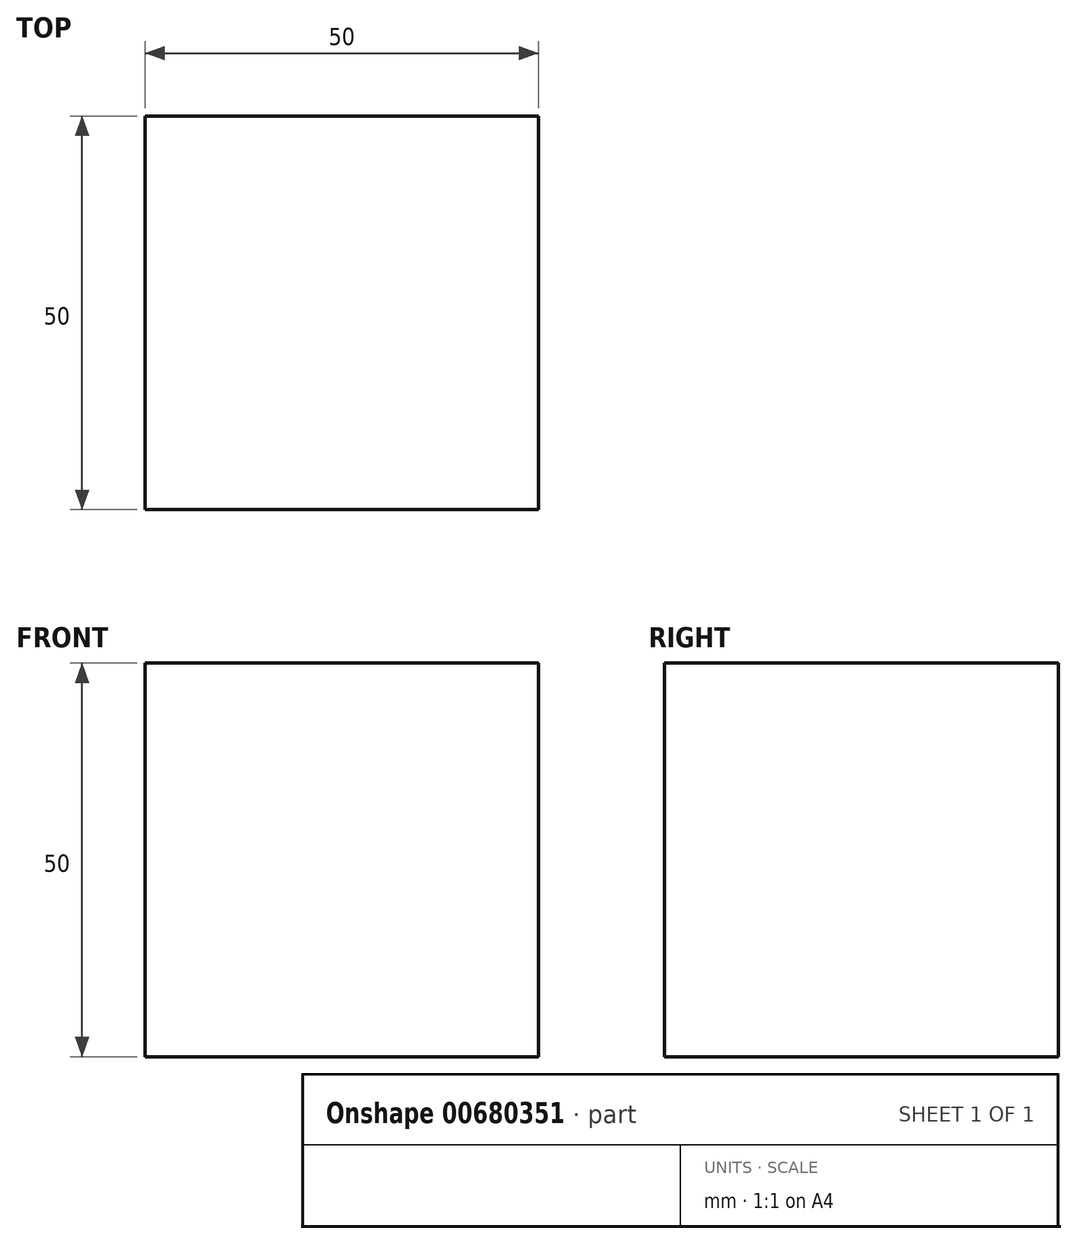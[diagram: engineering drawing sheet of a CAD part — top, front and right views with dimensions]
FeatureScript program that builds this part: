
annotation { "Feature Type Name" : "Feature", "Feature Type Description" : "" }
export const myFeature = defineFeature(function(context is Context, id is Id, definition is map)
    precondition{}
    {
        {
            var Q0;
            Q0=qCreatedBy(makeId("Top.planeOp"),FACE);
            var sketch = newSketch(context, id + "F0", { "sketchPlane" : qUnion([Q0])});
            skLineSegment(sketch, "E0.bottom", {"start": v(-22.73, 17.37) * mm, "end": v(27.27, 17.37) * mm});
            skLineSegment(sketch, "E0.top", {"start": v(-22.73, -32.63) * mm, "end": v(27.27, -32.63) * mm});
            skLineSegment(sketch, "E0.left", {"start": v(-22.73, 17.37) * mm, "end": v(-22.73, -32.63) * mm});
            skLineSegment(sketch, "E0.right", {"start": v(27.27, 17.37) * mm, "end": v(27.27, -32.63) * mm});
            skSolve(sketch);
        }
        {
            var Q0;
            Q0 = qSketchRegion(id + "F0", true);
            extrude(context, id + "F1", {"entities" : qUnion([Q0]), "depth" : 50 * mm, "offsetDistance" : 25 * mm});
        }
    });
